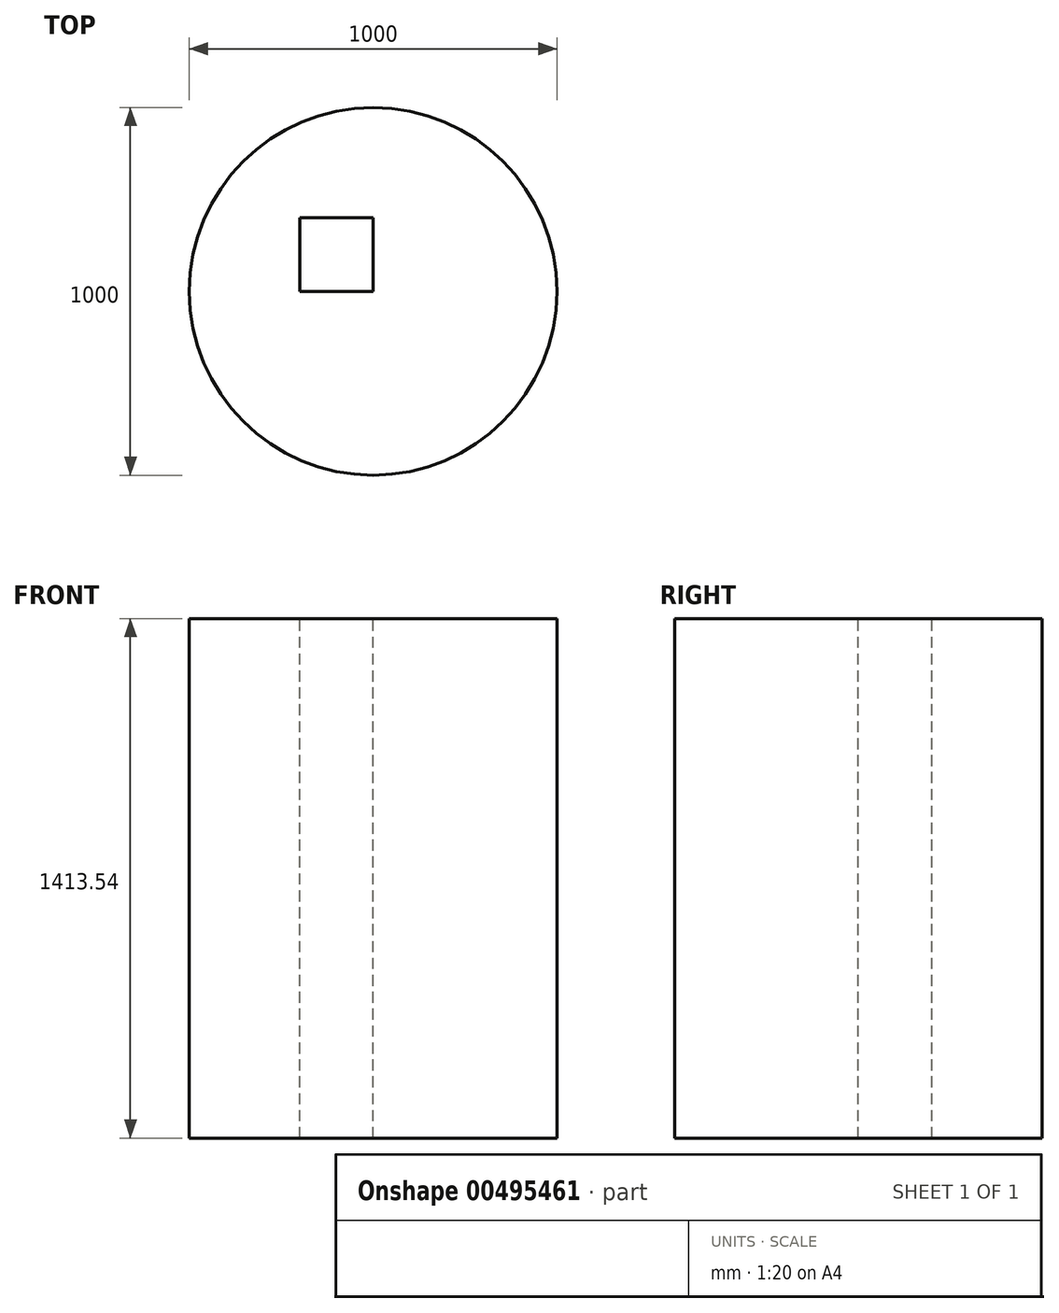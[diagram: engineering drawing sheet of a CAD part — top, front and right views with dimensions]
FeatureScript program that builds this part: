
annotation { "Feature Type Name" : "Feature", "Feature Type Description" : "" }
export const myFeature = defineFeature(function(context is Context, id is Id, definition is map)
    precondition{}
    {
        {
            var Q0;
            Q0=qCreatedBy(makeId("Top.planeOp"),FACE);
            var sketch = newSketch(context, id + "F0", { "sketchPlane" : qUnion([Q0])});
            skCircle(sketch, "E0", {"center": v(0, 0) * mm, "radius": 500 * mm});
            skSolve(sketch);
        }
        {
            var Q0;
            Q0=makeQuery(id+"F0.imprint","IMPRINT",FACE,{"disambiguationData":[TD([[makeQuery(id+"F0.imprint","IMPRINT",EDGE,{"derivedFrom":sQuery(id+"F0.wireOp",EDGE,"E0")}),1.0]])]});
            extrude(context, id + "F1", {"entities" : qUnion([Q0]), "depth" : 1413.54 * mm});
        }
        {
            var Q0;
            Q0=makeQuery(id+"F1.opExtrude","CAP_FACE",FACE,{"disambiguationData":[OSD([sQuery(id+"F0.wireOp",EDGE,"E0")])],"isStart":false});
            var sketch = newSketch(context, id + "F2", { "sketchPlane" : qUnion([Q0])});
            skLineSegment(sketch, "E1.bottom", {"start": v(0, 200) * mm, "end": v(-200, 200) * mm});
            skLineSegment(sketch, "E1.top", {"start": v(0, 0) * mm, "end": v(-200, 0) * mm});
            skLineSegment(sketch, "E1.left", {"start": v(0, 200) * mm, "end": v(0, 0) * mm});
            skLineSegment(sketch, "E1.right", {"start": v(-200, 200) * mm, "end": v(-200, 0) * mm});
            skLineSegment(sketch, "E2.bottom", {"start": v(-200, 200) * mm, "end": v(0, 200) * mm, "construction": true});
            skLineSegment(sketch, "E2.top", {"start": v(-200, 200) * mm, "end": v(0, 200) * mm, "construction": true});
            skLineSegment(sketch, "E2.left", {"start": v(-200, 200) * mm, "end": v(-200, 200) * mm});
            skLineSegment(sketch, "E2.right", {"start": v(0, 200) * mm, "end": v(0, 200) * mm});
            skSolve(sketch);
        }
        {
            var Q0;
            Q0 = qSketchRegion(id + "F2", true);
            extrude(context, id + "F3", {"entities" : qUnion([Q0]), "operationType" : NewBodyOperationType.REMOVE, "oppositeDirection" : true, "depth" : 2812.25 * mm});
        }
    });
